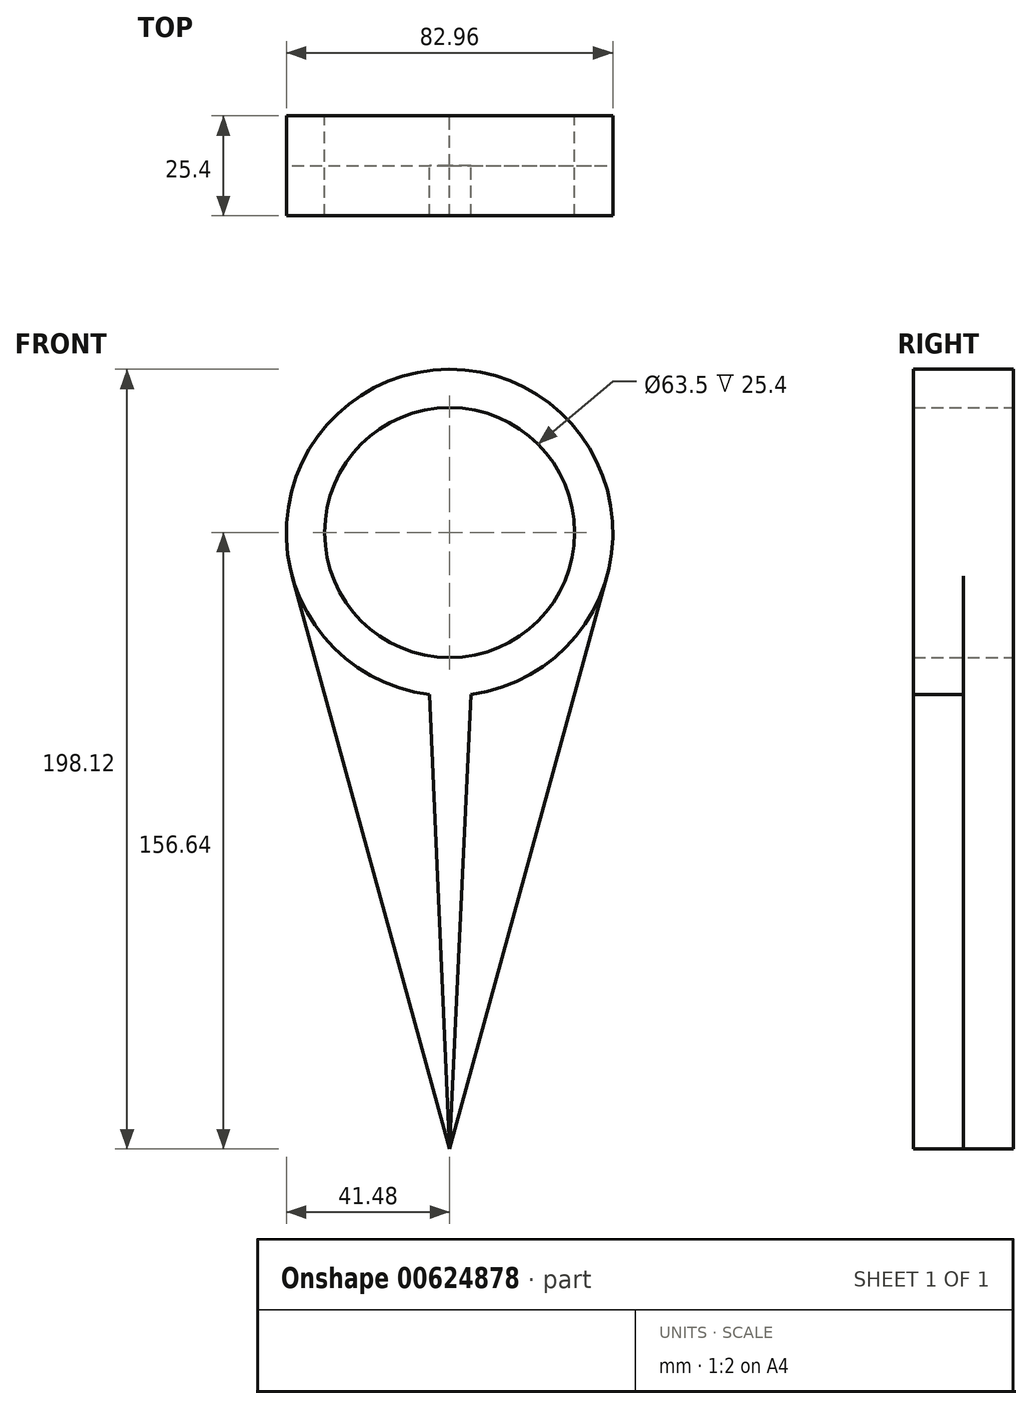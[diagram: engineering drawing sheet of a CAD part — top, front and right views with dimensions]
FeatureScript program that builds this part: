
annotation { "Feature Type Name" : "Feature", "Feature Type Description" : "" }
export const myFeature = defineFeature(function(context is Context, id is Id, definition is map)
    precondition{}
    {
        {
            var Q0;
            Q0=qCreatedBy(makeId("Front.planeOp"),FACE);
            var sketch = newSketch(context, id + "F0", { "sketchPlane" : qUnion([Q0])});
            skCircle(sketch, "E0", {"center": v(0, 0) * mm, "radius": 31.75 * mm});
            skCircle(sketch, "E1", {"center": v(0, 0) * mm, "radius": 41.48 * mm});
            skLineSegment(sketch, "E2", {"start": v(-40, -10.99) * mm, "end": v(0, -156.64) * mm});
            skLineSegment(sketch, "E3", {"start": v(0, -156.64) * mm, "end": v(40, -10.99) * mm});
            skSolve(sketch);
        }
        {
            var Q0;
            Q0=makeQuery(id+"F0.imprint","IMPRINT",FACE,{"disambiguationData":[TD([[makeQuery(id+"F0.imprint","IMPRINT",EDGE,{"derivedFrom":sQuery(id+"F0.wireOp",EDGE,"E0")}),-1.0]])]});
            extrude(context, id + "F1", {"entities" : qUnion([Q0]), "depth" : 25.4 * mm, "offsetDistance" : 25.4 * mm});
        }
        {
            var Q0;
            Q0 = qSketchRegion(id + "F0", true);
            extrude(context, id + "F2", {"entities" : qUnion([Q0]), "operationType" : NewBodyOperationType.ADD, "depth" : 12.7 * mm, "offsetDistance" : 25.4 * mm});
        }
        {
            var Q0;
            {var subQ0=sQuery(id+"F0.wireOp",EDGE,"E1");var subQ1=sQuery(id+"F0.wireOp",EDGE,"E0");Q0=makeQuery(id+"F2.boolean.opBoolean","MERGE",FACE,{"derivedFrom":[makeQuery(id+"F1.opExtrude","CAP_FACE",FACE,{"disambiguationData":[OSD([subQ1,subQ0])],"isStart":true}),makeQuery(id+"F2.opExtrude","CAP_FACE",FACE,{"disambiguationData":[OSD([subQ1,subQ0,sQuery(id+"F0.wireOp",EDGE,"E2"),sQuery(id+"F0.wireOp",EDGE,"E3")])],"isStart":true})]});}
            var sketch = newSketch(context, id + "F3", { "sketchPlane" : qUnion([Q0])});
            skLineSegment(sketch, "E4", {"start": v(-5.63, -37.11) * mm, "end": v(5.27, -37.11) * mm});
            skLineSegment(sketch, "E5", {"start": v(5.27, -37.11) * mm, "end": v(0, -156.64) * mm});
            skLineSegment(sketch, "E6", {"start": v(0, -156.64) * mm, "end": v(-5.63, -37.11) * mm});
            skSolve(sketch);
        }
        {
            var Q0;
            Q0 = qSketchRegion(id + "F3", true);
            extrude(context, id + "F4", {"entities" : qUnion([Q0]), "operationType" : NewBodyOperationType.ADD, "oppositeDirection" : true, "depth" : 25.4 * mm, "offsetDistance" : 25.4 * mm});
        }
    });
